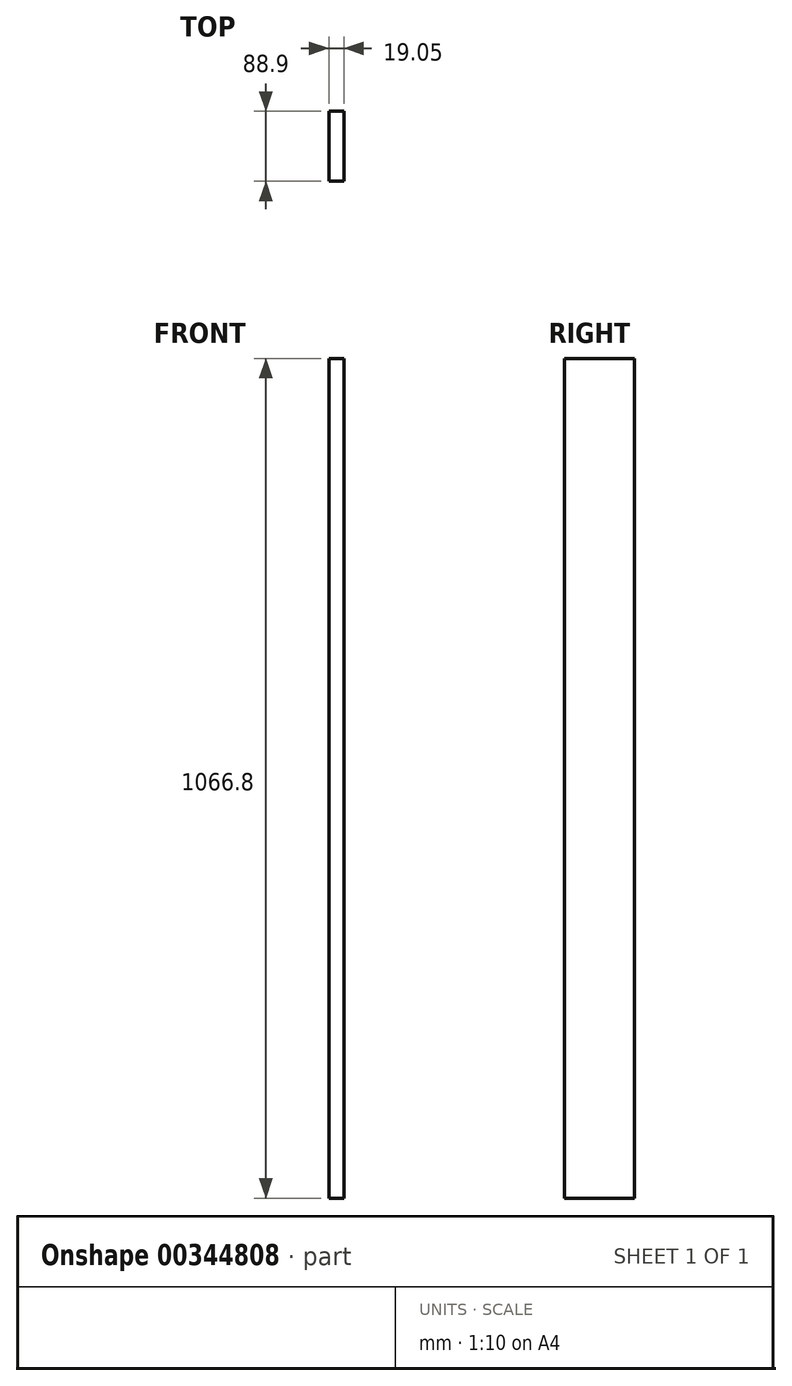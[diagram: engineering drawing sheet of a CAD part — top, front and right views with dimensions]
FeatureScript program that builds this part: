
annotation { "Feature Type Name" : "Feature", "Feature Type Description" : "" }
export const myFeature = defineFeature(function(context is Context, id is Id, definition is map)
    precondition{}
    {
        {
            var Q0;
            Q0=qCreatedBy(makeId("Right.planeOp"),FACE);
            var sketch = newSketch(context, id + "F0", { "sketchPlane" : qUnion([Q0])});
            skLineSegment(sketch, "E0.bottom", {"start": v(0, 0) * mm, "end": v(88.9, 0) * mm});
            skLineSegment(sketch, "E0.top", {"start": v(0, 1066.8) * mm, "end": v(88.9, 1066.8) * mm});
            skLineSegment(sketch, "E0.left", {"start": v(0, 0) * mm, "end": v(0, 1066.8) * mm});
            skLineSegment(sketch, "E0.right", {"start": v(88.9, 0) * mm, "end": v(88.9, 1066.8) * mm});
            skSolve(sketch);
        }
        {
            var Q0;
            Q0=makeQuery(id+"F0.imprint","IMPRINT",FACE,{"disambiguationData":[TD([[makeQuery(id+"F0.imprint","IMPRINT",EDGE,{"derivedFrom":sQuery(id+"F0.wireOp",EDGE,"E0.bottom")}),1.0]])]});
            extrude(context, id + "F1", {"entities" : qUnion([Q0]), "depth" : 19.05 * mm});
        }
    });
